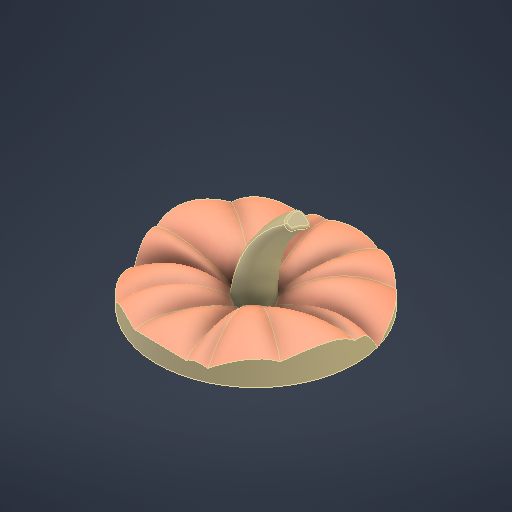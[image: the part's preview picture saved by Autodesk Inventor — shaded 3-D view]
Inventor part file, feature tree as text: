
AUTODESK INVENTOR PART (.ipt)
format: ipt  version: 2025.1 (Build 291241020, 241B)  size: 1,084,416 bytes
history: native  units: in
note: dims shown in document units (in); Inventor stores cm internally (conversion verified against a paired STEP export)
features: other x14, extrude x2, sketch x2
ambient origin geometry x8: Origin, YZ Plane, XZ Plane, XY Plane, X Axis, Y Axis, Z Axis, Center Point
bodies: Solid1 (feature_tree)
feature tree (18):
  other  "Axe1"
  other  "Plan1"
  other  "Plan2"
  other  "Plan3"
  other  "Plan4"
  other  "Plan5"
  other  "Plan6"
  other  "Plan7"
  other  "Plan8"
  other  "Plan9"
  other  "Plan10"
  other  "Plan11"
  other  "Plan12"
  extrude  "Extrusion1"  Depth=8.4562in TaperAngle=0.0deg
  extrude  "Extrusion2"  Depth=7.0866in
  sketch  "Sketch1"  dims[d0=7.874in d1=8.4562in d2=0.0in]
  sketch  "Sketch2"  dims[d3=7.0866in d4=9.0551in d5=0.1969in d6=1.5094in d7=0.0in d8=0.0in]
  other  "Enlèv. mat.-Extru.2"
